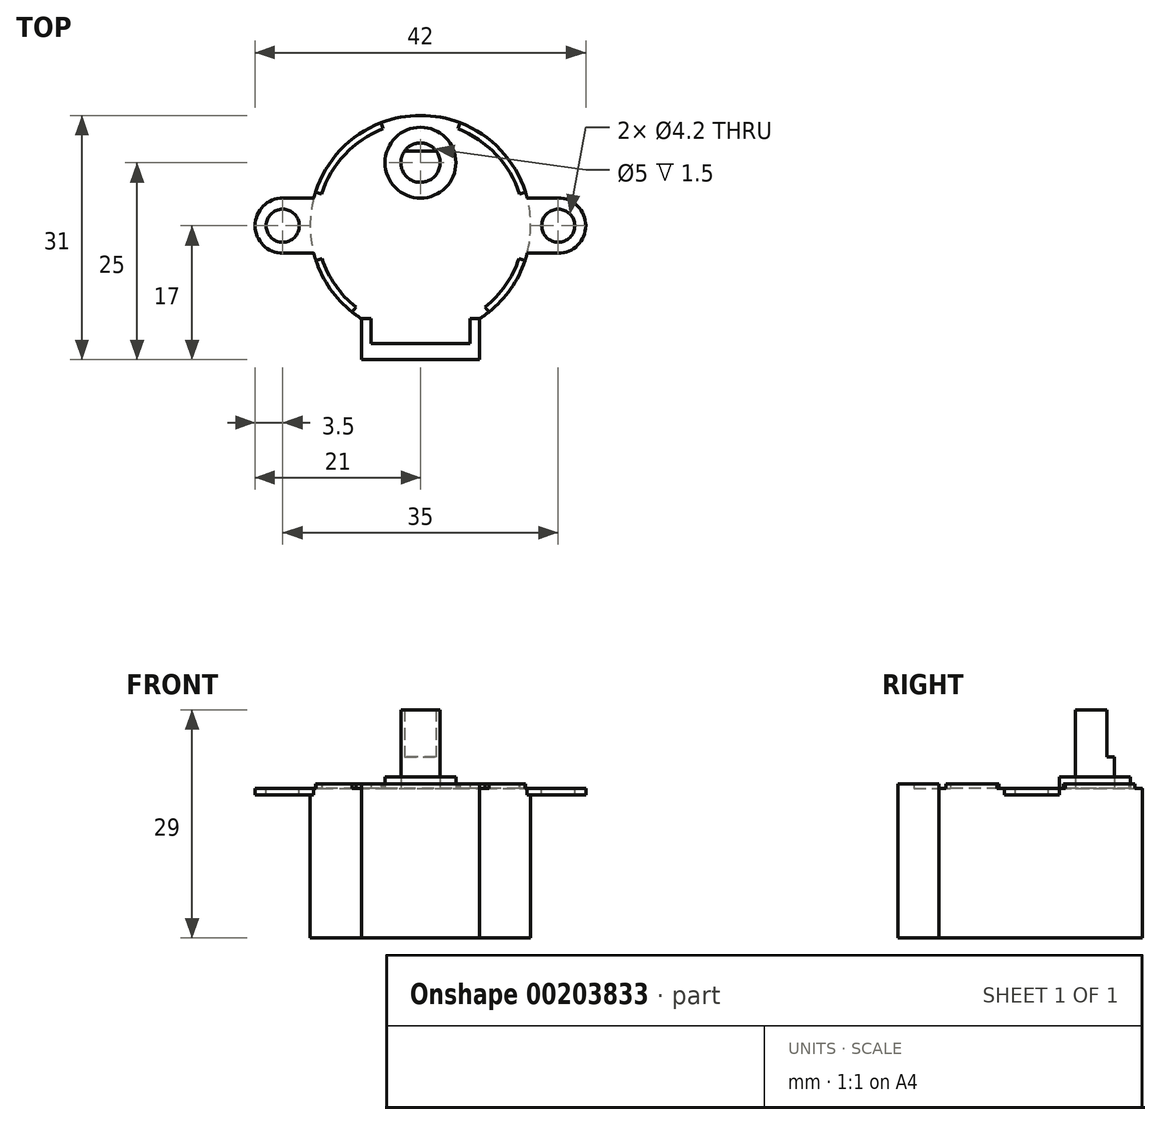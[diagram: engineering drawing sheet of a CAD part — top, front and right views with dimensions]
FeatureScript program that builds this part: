
annotation { "Feature Type Name" : "Feature", "Feature Type Description" : "" }
export const myFeature = defineFeature(function(context is Context, id is Id, definition is map)
    precondition{}
    {
        {
            var Q0;
            Q0=qCreatedBy(makeId("Top.planeOp"),FACE);
            var sketch = newSketch(context, id + "F0", { "sketchPlane" : qUnion([Q0])});
            skArc(sketch, "E0", {"start": v(7.5, -11.82) * mm, "mid": v(0, 14) * mm, "end": v(-7.5, -11.82) * mm});
            skCircle(sketch, "E1", {"center": v(-17.5, 0) * mm, "radius": 2.1 * mm});
            skCircle(sketch, "E2", {"center": v(17.5, 0) * mm, "radius": 2.1 * mm});
            skCircle(sketch, "E3", {"center": v(0, 8) * mm, "radius": 4.5 * mm});
            skArc(sketch, "E4", {"start": v(17.5, -3.5) * mm, "mid": v(21, 0) * mm, "end": v(17.5, 3.5) * mm});
            skArc(sketch, "E5", {"start": v(-17.5, 3.5) * mm, "mid": v(-21, 0) * mm, "end": v(-17.5, -3.5) * mm});
            skLineSegment(sketch, "E6", {"start": v(17.5, -3.5) * mm, "end": v(13.56, -3.5) * mm});
            skLineSegment(sketch, "E7", {"start": v(-17.5, 3.5) * mm, "end": v(-13.56, 3.5) * mm});
            skLineSegment(sketch, "E8.rect.bottom", {"start": v(7.5, -17) * mm, "end": v(-7.5, -17) * mm});
            skLineSegment(sketch, "E8.rect.left", {"start": v(7.5, -17) * mm, "end": v(7.5, -11.82) * mm});
            skLineSegment(sketch, "E8.rect.right", {"start": v(-7.5, -17) * mm, "end": v(-7.5, -11.82) * mm});
            skPoint(sketch, "E9.orphan", {"position": v(-7.5, 17) * mm});
            skPoint(sketch, "E10.orphan", {"position": v(7.5, 17) * mm});
            skLineSegment(sketch, "E11.trimOffspring", {"start": v(13.56, 3.5) * mm, "end": v(17.5, 3.5) * mm});
            skLineSegment(sketch, "E12.trimOffspring", {"start": v(-13.56, -3.5) * mm, "end": v(-17.5, -3.5) * mm});
            skCircle(sketch, "E13", {"center": v(0, 8) * mm, "radius": 2.5 * mm});
            skSolve(sketch);
        }
        {
            var Q0;
            Q0=makeQuery(id+"F0.imprint","IMPRINT",FACE,{"disambiguationData":[TD([[makeQuery(id+"F0.imprint","IMPRINT",EDGE,{"derivedFrom":sQuery(id+"F0.wireOp",EDGE,"E3")}),-1.0]])]});
            var Q1;
            Q1=makeQuery(id+"F0.imprint","IMPRINT",FACE,{"disambiguationData":[TD([[makeQuery(id+"F0.imprint","IMPRINT",EDGE,{"derivedFrom":sQuery(id+"F0.wireOp",EDGE,"E3")}),1.0]])]});
            var Q2;
            Q2=makeQuery(id+"F0.imprint","IMPRINT",FACE,{"disambiguationData":[TD([[makeQuery(id+"F0.imprint","IMPRINT",EDGE,{"derivedFrom":sQuery(id+"F0.wireOp",EDGE,"E13")}),1.0]])]});
            extrude(context, id + "F1", {"entities" : qUnion([Q0, Q1, Q2]), "depth" : 19 * mm});
        }
        {
            var Q0;
            Q0=makeQuery(id+"F0.imprint","IMPRINT",FACE,{"disambiguationData":[TD([[makeQuery(id+"F0.imprint","IMPRINT",EDGE,{"derivedFrom":sQuery(id+"F0.wireOp",EDGE,"E1")}),-1.0]])]});
            var Q1;
            Q1=makeQuery(id+"F0.imprint","IMPRINT",FACE,{"disambiguationData":[TD([[makeQuery(id+"F0.imprint","IMPRINT",EDGE,{"derivedFrom":sQuery(id+"F0.wireOp",EDGE,"E2")}),-1.0]])]});
            extrude(context, id + "F2", {"entities" : qUnion([Q0, Q1]), "operationType" : NewBodyOperationType.ADD, "depth" : 0.8 * mm});
        }
        {
            var Q0;
            Q0=makeQuery(id+"F0.imprint","IMPRINT",FACE,{"disambiguationData":[TD([[makeQuery(id+"F0.imprint","IMPRINT",EDGE,{"derivedFrom":sQuery(id+"F0.wireOp",EDGE,"E3")}),1.0]])]});
            extrude(context, id + "F3", {"entities" : qUnion([Q0]), "operationType" : NewBodyOperationType.ADD, "oppositeDirection" : true, "depth" : 1.5 * mm});
        }
        {
            var Q0;
            Q0=makeQuery(id+"F0.imprint","IMPRINT",FACE,{"disambiguationData":[TD([[makeQuery(id+"F0.imprint","IMPRINT",EDGE,{"derivedFrom":sQuery(id+"F0.wireOp",EDGE,"E13")}),1.0]])]});
            extrude(context, id + "F4", {"entities" : qUnion([Q0]), "oppositeDirection" : true, "depth" : 10 * mm});
        }
        {
            var Q0;
            Q0=makeQuery(id+"F4.opExtrude","CAP_FACE",FACE,{"disambiguationData":[OSD([sQuery(id+"F0.wireOp",EDGE,"E13")])],"isStart":false});
            var sketch = newSketch(context, id + "F5", { "sketchPlane" : qUnion([Q0])});
            skLineSegment(sketch, "E14.rect.bottom", {"start": v(2.91, -9.5) * mm, "end": v(-2.91, -9.5) * mm});
            skLineSegment(sketch, "E14.rect.top", {"start": v(2.91, -6.5) * mm, "end": v(-2.91, -6.5) * mm});
            skLineSegment(sketch, "E14.rect.left", {"start": v(2.91, -9.5) * mm, "end": v(2.91, -6.5) * mm});
            skLineSegment(sketch, "E14.rect.right", {"start": v(-2.91, -9.5) * mm, "end": v(-2.91, -6.5) * mm});
            skPoint(sketch, "E14.rect.middle", {"position": v(0, -8) * mm});
            skLineSegment(sketch, "E15.bottom", {"start": v(-2.91, -6.5) * mm, "end": v(2.91, -6.5) * mm});
            skLineSegment(sketch, "E15.top", {"start": v(-2.91, -5.02) * mm, "end": v(2.91, -5.02) * mm});
            skLineSegment(sketch, "E15.left", {"start": v(-2.91, -6.5) * mm, "end": v(-2.91, -5.02) * mm});
            skLineSegment(sketch, "E15.right", {"start": v(2.91, -6.5) * mm, "end": v(2.91, -5.02) * mm});
            skLineSegment(sketch, "E16.top", {"start": v(2.91, -10.83) * mm, "end": v(-2.91, -10.83) * mm});
            skLineSegment(sketch, "E16.left", {"start": v(2.91, -9.5) * mm, "end": v(2.91, -10.83) * mm});
            skLineSegment(sketch, "E16.right", {"start": v(-2.91, -9.5) * mm, "end": v(-2.91, -10.83) * mm});
            skSolve(sketch);
        }
        {
            var Q0;
            Q0=makeQuery(id+"F5.imprint","IMPRINT",FACE,{"disambiguationData":[TD([[makeQuery(id+"F5.imprint","IMPRINT",EDGE,{"derivedFrom":sQuery(id+"F5.wireOp",EDGE,"E15.top")}),-1.0]])]});
            var Q1;
            {var subQ0=makeQuery(id+"F4.opExtrude","CAP_EDGE",EDGE,{"disambiguationData":[OSD([sQuery(id+"F0.wireOp",EDGE,"E13")])],"isStart":false});var subQ1=sQuery(id+"F5.wireOp",EDGE,"E15.bottom");var subQ3=makeQuery(id+"F5.imprint","INTERSECT",VERTEX,{"disambiguationData":[OD(0.0)],"derivedFrom":[subQ0,subQ1]});Q1=makeQuery(id+"F5.imprint","IMPRINT",FACE,{"disambiguationData":[TD([[makeQuery(id+"F5.imprint","IMPRINT",EDGE,{"disambiguationData":[TD([[subQ3,-1.0]])],"derivedFrom":subQ1}),1.0]])]});}
            var Q2;
            {var subQ0=makeQuery(id+"F4.opExtrude","CAP_EDGE",EDGE,{"disambiguationData":[OSD([sQuery(id+"F0.wireOp",EDGE,"E13")])],"isStart":false});var subQ1=sQuery(id+"F5.wireOp",EDGE,"E14.rect.bottom");var subQ3=makeQuery(id+"F5.imprint","INTERSECT",VERTEX,{"disambiguationData":[OD(0.0)],"derivedFrom":[subQ0,subQ1]});Q2=makeQuery(id+"F5.imprint","IMPRINT",FACE,{"disambiguationData":[TD([[makeQuery(id+"F5.imprint","IMPRINT",EDGE,{"disambiguationData":[TD([[subQ3,-1.0]])],"derivedFrom":subQ1}),1.0]])]});}
            var Q3;
            Q3=makeQuery(id+"F5.imprint","IMPRINT",FACE,{"disambiguationData":[TD([[makeQuery(id+"F5.imprint","IMPRINT",EDGE,{"derivedFrom":sQuery(id+"F5.wireOp",EDGE,"E16.top")}),-1.0]])]});
            extrude(context, id + "F6", {"entities" : qUnion([Q0, Q1, Q2, Q3]), "oppositeDirection" : true, "depth" : 6 * mm});
        }
        {
            var Q0;
            Q0=makeQuery(id+"F6.opExtrude","SWEPT_BODY",BODY,{"disambiguationData":[OSD([sQuery(id+"F5.wireOp",EDGE,"E15.bottom"),sQuery(id+"F5.wireOp",EDGE,"E15.top"),sQuery(id+"F5.wireOp",EDGE,"E15.left"),sQuery(id+"F5.wireOp",EDGE,"E15.right")])]});
            var Q1;
            Q1=makeQuery(id+"F6.opExtrude","SWEPT_BODY",BODY,{"disambiguationData":[OSD([sQuery(id+"F5.wireOp",EDGE,"E14.rect.bottom"),sQuery(id+"F5.wireOp",EDGE,"E16.top"),sQuery(id+"F5.wireOp",EDGE,"E16.left"),sQuery(id+"F5.wireOp",EDGE,"E16.right")])]});
            var Q2;
            Q2=makeQuery(id+"F4.opExtrude","SWEPT_BODY",BODY,{"disambiguationData":[OSD([sQuery(id+"F0.wireOp",EDGE,"E13")])]});
            booleanBodies(context, id + "F7", {"operationType" : BooleanOperationType.SUBTRACTION, "tools" : qUnion([Q0, Q1]), "targets" : qUnion([Q2])});
        }
        {
            var Q0;
            Q0=makeQuery(id+"F0.imprint","IMPRINT",FACE,{"disambiguationData":[TD([[makeQuery(id+"F0.imprint","IMPRINT",EDGE,{"derivedFrom":sQuery(id+"F0.wireOp",EDGE,"E3")}),-1.0]])]});
            var sketch = newSketch(context, id + "F8", { "sketchPlane" : qUnion([Q0])});
            skArc(sketch, "E17", {"start": v(-12.51, -4.2) * mm, "mid": v(-10.8, -7.58) * mm, "end": v(-8.22, -10.33) * mm});
            skArc(sketch, "E18", {"start": v(-13.27, -4.45) * mm, "mid": v(-11.46, -8.04) * mm, "end": v(-8.71, -10.96) * mm});
            skLineSegment(sketch, "E19", {"start": v(-8.71, -10.96) * mm, "end": v(-8.22, -10.33) * mm});
            skLineSegment(sketch, "E20", {"start": v(-13.27, -4.45) * mm, "end": v(-12.51, -4.2) * mm});
            skLineSegment(sketch, "E21", {"start": v(-12.58, 4) * mm, "end": v(-13.34, 4.25) * mm});
            skLineSegment(sketch, "E22", {"start": v(-4.75, 12.32) * mm, "end": v(-5.04, 13.06) * mm});
            skLineSegment(sketch, "E23.MirrorCS", {"start": v(4.75, 12.32) * mm, "end": v(5.04, 13.06) * mm});
            skLineSegment(sketch, "E24.MirrorCS", {"start": v(12.58, 4) * mm, "end": v(13.34, 4.25) * mm});
            skLineSegment(sketch, "E25.MirrorCS", {"start": v(8.71, -10.96) * mm, "end": v(8.22, -10.33) * mm});
            skLineSegment(sketch, "E26.MirrorCS", {"start": v(13.27, -4.45) * mm, "end": v(12.51, -4.2) * mm});
            skArc(sketch, "E27.trimOffspring", {"start": v(8.71, -10.96) * mm, "mid": v(11.46, -8.04) * mm, "end": v(13.27, -4.45) * mm});
            skArc(sketch, "E28.trimOffspring", {"start": v(8.22, -10.33) * mm, "mid": v(10.8, -7.58) * mm, "end": v(12.51, -4.2) * mm});
            skArc(sketch, "E29.trimOffspring", {"start": v(13.34, 4.25) * mm, "mid": v(10.2, 9.6) * mm, "end": v(5.04, 13.06) * mm});
            skArc(sketch, "E30.trimOffspring", {"start": v(12.58, 4) * mm, "mid": v(9.6, 9.05) * mm, "end": v(4.75, 12.32) * mm});
            skArc(sketch, "E31.trimOffspring", {"start": v(-4.75, 12.32) * mm, "mid": v(-9.6, 9.05) * mm, "end": v(-12.58, 4) * mm});
            skArc(sketch, "E32.trimOffspring", {"start": v(-5.04, 13.06) * mm, "mid": v(-10.2, 9.6) * mm, "end": v(-13.34, 4.25) * mm});
            skLineSegment(sketch, "E33", {"start": v(-6.3, -15) * mm, "end": v(6.3, -15) * mm});
            skLineSegment(sketch, "E34", {"start": v(6.3, -15) * mm, "end": v(6.3, -11.82) * mm});
            skLineSegment(sketch, "E35", {"start": v(6.3, -11.82) * mm, "end": v(7.5, -11.82) * mm});
            skLineSegment(sketch, "E36", {"start": v(7.5, -11.82) * mm, "end": v(7.5, -17) * mm});
            skLineSegment(sketch, "E37", {"start": v(7.5, -17) * mm, "end": v(-7.5, -17) * mm});
            skLineSegment(sketch, "E38", {"start": v(-7.5, -17) * mm, "end": v(-7.5, -11.82) * mm});
            skLineSegment(sketch, "E39", {"start": v(-7.5, -11.82) * mm, "end": v(-6.3, -11.82) * mm});
            skLineSegment(sketch, "E40", {"start": v(-6.3, -11.82) * mm, "end": v(-6.3, -15) * mm});
            skSolve(sketch);
        }
        {
            var Q0;
            Q0 = qSketchRegion(id + "F8", true);
            extrude(context, id + "F9", {"entities" : qUnion([Q0]), "operationType" : NewBodyOperationType.ADD, "oppositeDirection" : true, "depth" : 0.6 * mm});
        }
        {
            var Q0;
            Q0=makeQuery(id+"F1.opExtrude","SWEPT_BODY",BODY,{"disambiguationData":[OSD([sQuery(id+"F0.wireOp",EDGE,"E0"),sQuery(id+"F0.wireOp",EDGE,"E8.rect.bottom"),sQuery(id+"F0.wireOp",EDGE,"E8.rect.left"),sQuery(id+"F0.wireOp",EDGE,"E8.rect.right")])]});
            var Q1;
            Q1=makeQuery(id+"F4.opExtrude","SWEPT_BODY",BODY,{"disambiguationData":[OSD([sQuery(id+"F0.wireOp",EDGE,"E13")])]});
            var Q2;
            Q2=makeQuery(id+"F9.opExtrude","CAP_EDGE",EDGE,{"disambiguationData":[OSD([sQuery(id+"F8.wireOp",EDGE,"E36")])],"isStart":false});
            transform(context, id + "F10", {"entities" : qUnion([Q0, Q1]), "transformType" : TransformType.ROTATION, "transformAxis" : qUnion([Q2]), "angle" : 180 * degree, "makeCopy" : false});
        }
    });
